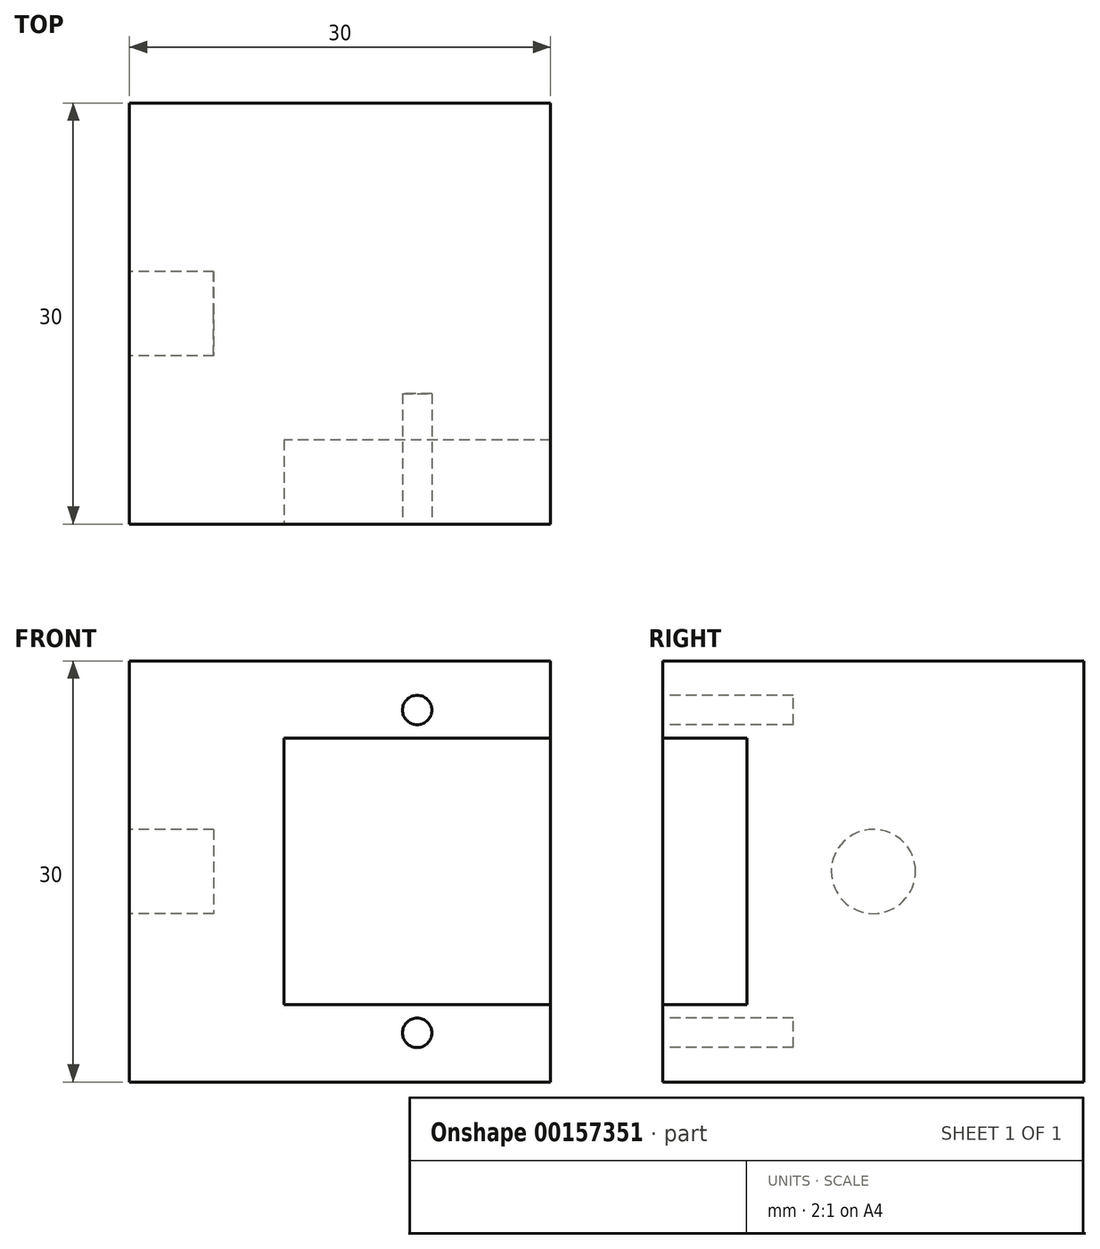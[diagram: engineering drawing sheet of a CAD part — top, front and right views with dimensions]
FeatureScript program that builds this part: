
annotation { "Feature Type Name" : "Feature", "Feature Type Description" : "" }
export const myFeature = defineFeature(function(context is Context, id is Id, definition is map)
    precondition{}
    {
        {
            var Q0;
            Q0=qCreatedBy(makeId("Right.planeOp"),FACE);
            var sketch = newSketch(context, id + "F0", { "sketchPlane" : qUnion([Q0])});
            skLineSegment(sketch, "E0.bottom", {"start": v(15, 15) * mm, "end": v(-15, 15) * mm});
            skLineSegment(sketch, "E0.top", {"start": v(15, -15) * mm, "end": v(-15, -15) * mm});
            skLineSegment(sketch, "E0.left", {"start": v(15, 15) * mm, "end": v(15, -15) * mm});
            skLineSegment(sketch, "E0.right", {"start": v(-15, 15) * mm, "end": v(-15, -15) * mm});
            skPoint(sketch, "E0.middle", {"position": v(0, 0) * mm});
            skSolve(sketch);
        }
        {
            var Q0;
            Q0=makeQuery(id+"F0.imprint","IMPRINT",FACE,{"disambiguationData":[TD([[makeQuery(id+"F0.imprint","IMPRINT",EDGE,{"derivedFrom":sQuery(id+"F0.wireOp",EDGE,"E0.bottom")}),1.0]])]});
            extrude(context, id + "F1", {"entities" : qUnion([Q0]), "depth" : 30 * mm});
        }
        {
            var Q0;
            Q0=makeQuery(id+"F1.opExtrude","CAP_FACE",FACE,{"disambiguationData":[OSD([sQuery(id+"F0.wireOp",EDGE,"E0.bottom"),sQuery(id+"F0.wireOp",EDGE,"E0.top"),sQuery(id+"F0.wireOp",EDGE,"E0.left"),sQuery(id+"F0.wireOp",EDGE,"E0.right")])],"isStart":true});
            var sketch = newSketch(context, id + "F2", { "sketchPlane" : qUnion([Q0])});
            skCircle(sketch, "E1", {"center": v(0, 0) * mm, "radius": 3 * mm});
            skSolve(sketch);
        }
        {
            var Q0;
            Q0=makeQuery(id+"F2.imprint","IMPRINT",FACE,{"disambiguationData":[TD([[makeQuery(id+"F2.imprint","IMPRINT",EDGE,{"derivedFrom":sQuery(id+"F2.wireOp",EDGE,"E1")}),1.0]])]});
            extrude(context, id + "F3", {"entities" : qUnion([Q0]), "operationType" : NewBodyOperationType.REMOVE, "oppositeDirection" : true, "depth" : 6 * mm});
        }
        {
            var Q0;
            Q0=makeQuery(id+"F1.opExtrude","SWEPT_FACE",FACE,{"disambiguationData":[OSD([sQuery(id+"F0.wireOp",EDGE,"E0.right")])]});
            var sketch = newSketch(context, id + "F4", { "sketchPlane" : qUnion([Q0])});
            skLineSegment(sketch, "E2.bottom", {"start": v(30, 9.5) * mm, "end": v(11, 9.5) * mm});
            skLineSegment(sketch, "E2.top", {"start": v(30, -9.5) * mm, "end": v(11, -9.5) * mm});
            skLineSegment(sketch, "E2.left", {"start": v(30, 9.5) * mm, "end": v(30, -9.5) * mm});
            skLineSegment(sketch, "E2.right", {"start": v(11, 9.5) * mm, "end": v(11, -9.5) * mm});
            skSolve(sketch);
        }
        {
            var Q0;
            Q0=makeQuery(id+"F4.imprint","IMPRINT",FACE,{"disambiguationData":[TD([[makeQuery(id+"F4.imprint","IMPRINT",EDGE,{"derivedFrom":sQuery(id+"F4.wireOp",EDGE,"E2.bottom")}),1.0]])]});
            extrude(context, id + "F5", {"entities" : qUnion([Q0]), "operationType" : NewBodyOperationType.REMOVE, "oppositeDirection" : true, "depth" : 6 * mm});
        }
        {
            var Q0;
            Q0=makeQuery(id+"F1.opExtrude","SWEPT_FACE",FACE,{"disambiguationData":[OSD([sQuery(id+"F0.wireOp",EDGE,"E0.right")])]});
            var sketch = newSketch(context, id + "F6", { "sketchPlane" : qUnion([Q0])});
            skCircle(sketch, "E3", {"center": v(20.5, 11.5) * mm, "radius": 1.05 * mm});
            skCircle(sketch, "E4", {"center": v(20.5, -11.5) * mm, "radius": 1.05 * mm});
            skSolve(sketch);
        }
        {
            var Q0;
            Q0=makeQuery(id+"F6.imprint","IMPRINT",FACE,{"disambiguationData":[TD([[makeQuery(id+"F6.imprint","IMPRINT",EDGE,{"derivedFrom":sQuery(id+"F6.wireOp",EDGE,"E3")}),1.0]])]});
            var Q1;
            Q1=makeQuery(id+"F6.imprint","IMPRINT",FACE,{"disambiguationData":[TD([[makeQuery(id+"F6.imprint","IMPRINT",EDGE,{"derivedFrom":sQuery(id+"F6.wireOp",EDGE,"E4")}),1.0]])]});
            extrude(context, id + "F7", {"entities" : qUnion([Q0, Q1]), "operationType" : NewBodyOperationType.REMOVE, "oppositeDirection" : true, "depth" : 9.3 * mm});
        }
    });
